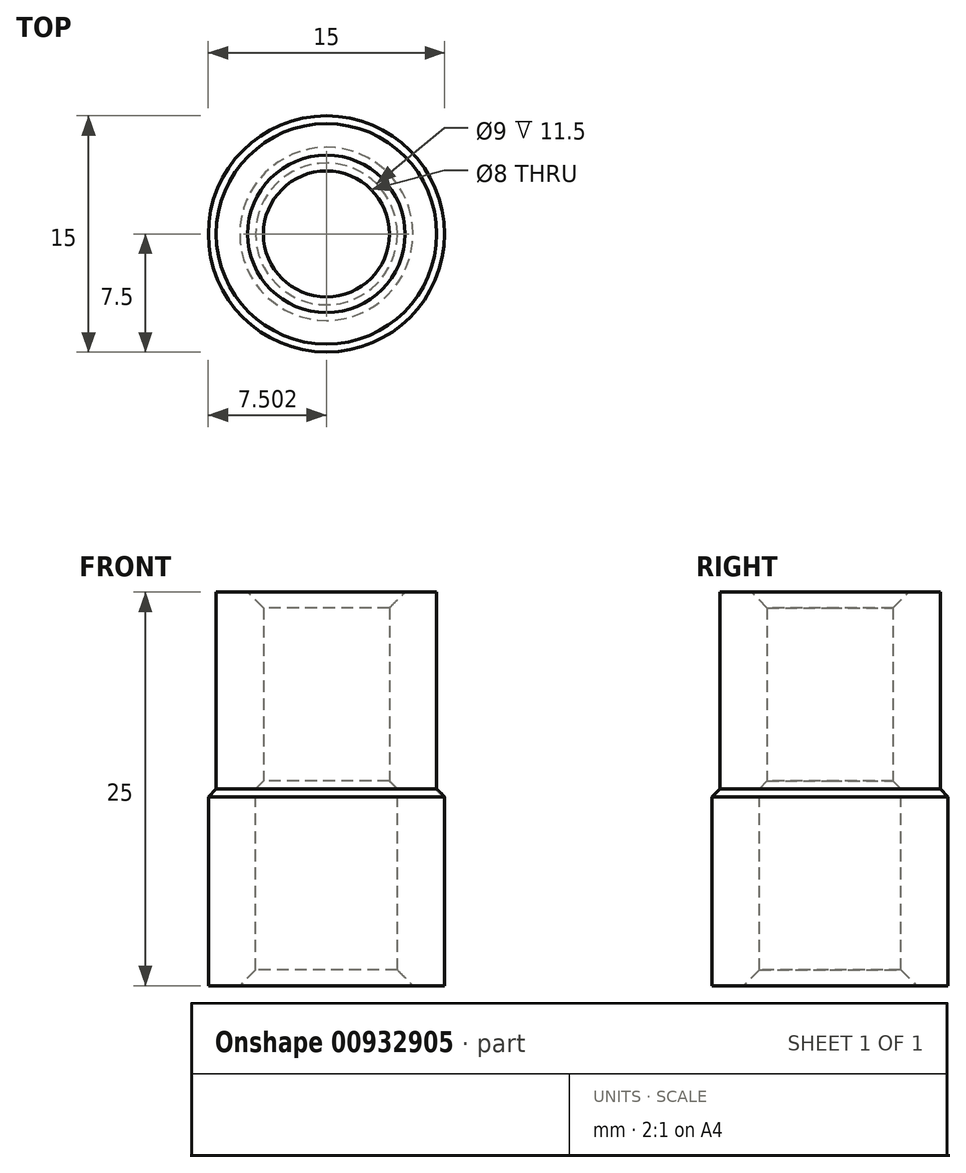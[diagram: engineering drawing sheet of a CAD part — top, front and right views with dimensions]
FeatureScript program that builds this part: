
annotation { "Feature Type Name" : "Feature", "Feature Type Description" : "" }
export const myFeature = defineFeature(function(context is Context, id is Id, definition is map)
    precondition{}
    {
        {
            var Q0;
            Q0=qCreatedBy(makeId("Top.planeOp"),FACE);
            var sketch = newSketch(context, id + "F0", { "sketchPlane" : qUnion([Q0])});
            skCircle(sketch, "E0", {"center": v(6.7, 0) * mm, "radius": 4 * mm});
            skCircle(sketch, "E1", {"center": v(6.7, 0) * mm, "radius": 7 * mm});
            skCircle(sketch, "E2", {"center": v(6.7, 0) * mm, "radius": 4.5 * mm});
            skCircle(sketch, "E3", {"center": v(6.7, 0) * mm, "radius": 7.5 * mm});
            skSolve(sketch);
        }
        {
            var Q0;
            Q0=makeQuery(id+"F0.imprint","IMPRINT",FACE,{"disambiguationData":[TD([[makeQuery(id+"F0.imprint","IMPRINT",EDGE,{"derivedFrom":sQuery(id+"F0.wireOp",EDGE,"E1")}),1.0]])]});
            var Q1;
            Q1=makeQuery(id+"F0.imprint","IMPRINT",FACE,{"disambiguationData":[TD([[makeQuery(id+"F0.imprint","IMPRINT",EDGE,{"derivedFrom":sQuery(id+"F0.wireOp",EDGE,"E0")}),-1.0]])]});
            var Q2;
            Q2=sQuery(id+"F0.wireOp",EDGE,"E0");
            var Q3;
            Q3=sQuery(id+"F0.wireOp",EDGE,"E2");
            var Q4;
            Q4=sQuery(id+"F0.wireOp",EDGE,"E1");
            extrude(context, id + "F1", {"entities" : qUnion([Q0, Q1]), "surfaceOperationType" : NewSurfaceOperationType.ADD, "surfaceEntities" : qUnion([Q2, Q3, Q4]), "depth" : 12.5 * mm, "offsetDistance" : 25 * mm});
        }
        {
            var Q0;
            Q0=makeQuery(id+"F0.imprint","IMPRINT",FACE,{"disambiguationData":[TD([[makeQuery(id+"F0.imprint","IMPRINT",EDGE,{"derivedFrom":sQuery(id+"F0.wireOp",EDGE,"E1")}),-1.0]])]});
            var Q1;
            Q1=makeQuery(id+"F0.imprint","IMPRINT",FACE,{"disambiguationData":[TD([[makeQuery(id+"F0.imprint","IMPRINT",EDGE,{"derivedFrom":sQuery(id+"F0.wireOp",EDGE,"E1")}),1.0]])]});
            var Q2;
            Q2=sQuery(id+"F0.wireOp",EDGE,"E3");
            var Q3;
            Q3=sQuery(id+"F0.wireOp",EDGE,"E1");
            var Q4;
            Q4=sQuery(id+"F0.wireOp",EDGE,"E2");
            extrude(context, id + "F2", {"entities" : qUnion([Q0, Q1]), "surfaceEntities" : qUnion([Q2, Q3, Q4]), "oppositeDirection" : true, "depth" : 12.5 * mm, "offsetDistance" : 25 * mm});
        }
        {
            var Q0;
            Q0=makeQuery(id+"F1.opExtrude","CAP_EDGE",EDGE,{"disambiguationData":[OSD([sQuery(id+"F0.wireOp",EDGE,"E0")])],"isStart":true});
            var Q1;
            Q1=makeQuery(id+"F2.opExtrude","CAP_EDGE",EDGE,{"disambiguationData":[OSD([sQuery(id+"F0.wireOp",EDGE,"E3")])],"isStart":true});
            chamfer(context, id + "F3", {"entities" : qUnion([Q0, Q1]), "width" : .5 * mm, "tangentPropagation" : true});
        }
        {
            var Q0;
            Q0=makeQuery(id+"F2.opExtrude","CAP_EDGE",EDGE,{"disambiguationData":[OSD([sQuery(id+"F0.wireOp",EDGE,"E2")])],"isStart":false});
            var Q1;
            Q1=makeQuery(id+"F1.opExtrude","CAP_EDGE",EDGE,{"disambiguationData":[OSD([sQuery(id+"F0.wireOp",EDGE,"E0")])],"isStart":false});
            chamfer(context, id + "F4", {"entities" : qUnion([Q0, Q1]), "width" : 1 * mm, "tangentPropagation" : true});
        }
    });
